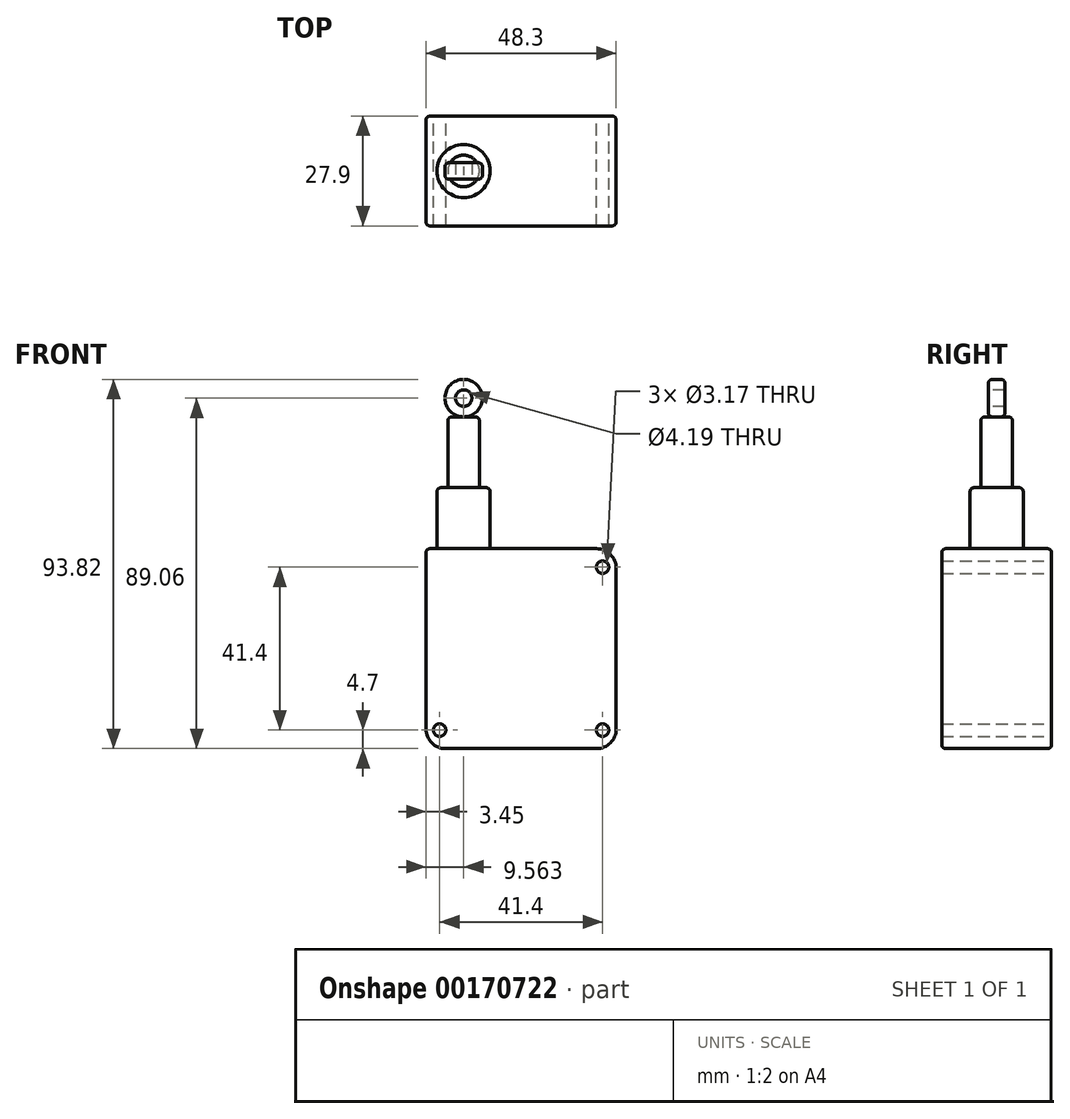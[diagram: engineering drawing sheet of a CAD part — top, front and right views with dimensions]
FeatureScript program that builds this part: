
annotation { "Feature Type Name" : "Feature", "Feature Type Description" : "" }
export const myFeature = defineFeature(function(context is Context, id is Id, definition is map)
    precondition{}
    {
        {
            var Q0;
            Q0=qCreatedBy(makeId("Front.planeOp"),FACE);
            var sketch = newSketch(context, id + "F0", { "sketchPlane" : qUnion([Q0])});
            skLineSegment(sketch, "E0.bottom", {"start": v(24.15, 25.4) * mm, "end": v(-24.15, 25.4) * mm});
            skLineSegment(sketch, "E0.top", {"start": v(24.15, -25.4) * mm, "end": v(-24.15, -25.4) * mm});
            skLineSegment(sketch, "E0.left", {"start": v(24.15, 25.4) * mm, "end": v(24.15, -25.4) * mm});
            skLineSegment(sketch, "E0.right", {"start": v(-24.15, 25.4) * mm, "end": v(-24.15, -25.4) * mm});
            skPoint(sketch, "E0.middle", {"position": v(0, 0) * mm});
            skLineSegment(sketch, "E1.bottom", {"start": v(20.7, 20.7) * mm, "end": v(-20.7, 20.7) * mm});
            skLineSegment(sketch, "E1.top", {"start": v(20.7, -20.7) * mm, "end": v(-20.7, -20.7) * mm});
            skLineSegment(sketch, "E1.left", {"start": v(20.7, 20.7) * mm, "end": v(20.7, -20.7) * mm});
            skLineSegment(sketch, "E1.right", {"start": v(-20.7, 20.7) * mm, "end": v(-20.7, -20.7) * mm});
            skCircle(sketch, "E2", {"center": v(20.7, -20.7) * mm, "radius": 1.59 * mm});
            skCircle(sketch, "E3", {"center": v(-20.7, -20.7) * mm, "radius": 1.59 * mm});
            skCircle(sketch, "E4", {"center": v(20.7, 20.7) * mm, "radius": 1.59 * mm});
            skLineSegment(sketch, "E5", {"start": v(-14.6, -30.38) * mm, "end": v(-14.6, 42.52) * mm});
            skSolve(sketch);
        }
        {
            var Q0;
            Q0 = qSketchRegion(id + "F0", true);
            var Q1;
            {var subQ3=sQuery(id+"F0.wireOp",EDGE,"E1.right");var subQ5=sQuery(id+"F0.wireOp",EDGE,"E1.bottom");var subQ6=makeQuery(id+"F0.imprint","INTERSECT",VERTEX,{"derivedFrom":[subQ5,subQ3]});Q1=makeQuery(id+"F0.imprint","IMPRINT",FACE,{"disambiguationData":[TD([[makeQuery(id+"F0.imprint","IMPRINT",EDGE,{"disambiguationData":[TD([[subQ6,1.0]])],"derivedFrom":subQ5}),1.0]])]});}
            var Q2;
            {var subQ5=sQuery(id+"F0.wireOp",EDGE,"E4");var subQ7=sQuery(id+"F0.wireOp",EDGE,"E1.bottom");var subQ8=makeQuery(id+"F0.imprint","INTERSECT",VERTEX,{"derivedFrom":[subQ7,subQ5]});Q2=makeQuery(id+"F0.imprint","IMPRINT",FACE,{"disambiguationData":[TD([[makeQuery(id+"F0.imprint","IMPRINT",EDGE,{"disambiguationData":[TD([[subQ8,-1.0]])],"derivedFrom":subQ7}),1.0]])]});}
            extrude(context, id + "F1", {"entities" : qUnion([Q0, Q1, Q2]), "depth" : 27.9 * mm});
        }
        {
            var Q0;
            Q0=makeQuery(id+"F1.opExtrude","SWEPT_FACE",FACE,{"disambiguationData":[OSD([sQuery(id+"F0.wireOp",EDGE,"E0.bottom")])]});
            var sketch = newSketch(context, id + "F2", { "sketchPlane" : qUnion([Q0])});
            skLineSegment(sketch, "E6", {"start": v(-14.6, 19.18) * mm, "end": v(-14.6, -45.39) * mm});
            skLineSegment(sketch, "E7", {"start": v(24.15, -13.95) * mm, "end": v(-48.5, -13.95) * mm});
            skPoint(sketch, "E7.endSnap0", {"position": v(24.15, -13.95) * mm});
            skCircle(sketch, "E8", {"center": v(-14.6, -13.95) * mm, "radius": 6.75 * mm});
            skSolve(sketch);
        }
        {
            var Q0;
            {var subQ0=sQuery(id+"F2.wireOp",EDGE,"E8");var subQ1=sQuery(id+"F2.wireOp",EDGE,"E6");var subQ2=makeQuery(id+"F2.imprint","INTERSECT",VERTEX,{"disambiguationData":[OD(0.0)],"derivedFrom":[subQ1,subQ0]});Q0=makeQuery(id+"F2.imprint","IMPRINT",FACE,{"disambiguationData":[TD([[makeQuery(id+"F2.imprint","IMPRINT",EDGE,{"disambiguationData":[TD([[subQ2,-1.0]])],"derivedFrom":subQ1}),-1.0]])]});}
            var Q1;
            {var subQ0=sQuery(id+"F2.wireOp",EDGE,"E8");var subQ1=sQuery(id+"F2.wireOp",EDGE,"E6");var subQ2=makeQuery(id+"F2.imprint","INTERSECT",VERTEX,{"disambiguationData":[OD(0.0)],"derivedFrom":[subQ1,subQ0]});Q1=makeQuery(id+"F2.imprint","IMPRINT",FACE,{"disambiguationData":[TD([[makeQuery(id+"F2.imprint","IMPRINT",EDGE,{"disambiguationData":[TD([[subQ2,-1.0]])],"derivedFrom":subQ1}),1.0]])]});}
            var Q2;
            {var subQ0=sQuery(id+"F2.wireOp",EDGE,"E7");var subQ1=sQuery(id+"F2.wireOp",EDGE,"E6");var subQ2=makeQuery(id+"F2.imprint","INTERSECT",VERTEX,{"derivedFrom":[subQ1,subQ0]});Q2=makeQuery(id+"F2.imprint","IMPRINT",FACE,{"disambiguationData":[TD([[makeQuery(id+"F2.imprint","IMPRINT",EDGE,{"disambiguationData":[TD([[subQ2,-1.0]])],"derivedFrom":subQ1}),1.0]])]});}
            var Q3;
            {var subQ0=sQuery(id+"F2.wireOp",EDGE,"E7");var subQ1=sQuery(id+"F2.wireOp",EDGE,"E6");var subQ2=makeQuery(id+"F2.imprint","INTERSECT",VERTEX,{"derivedFrom":[subQ1,subQ0]});Q3=makeQuery(id+"F2.imprint","IMPRINT",FACE,{"disambiguationData":[TD([[makeQuery(id+"F2.imprint","IMPRINT",EDGE,{"disambiguationData":[TD([[subQ2,-1.0]])],"derivedFrom":subQ1}),-1.0]])]});}
            extrude(context, id + "F3", {"entities" : qUnion([Q0, Q1, Q2, Q3]), "operationType" : NewBodyOperationType.ADD, "depth" : 15.5 * mm});
        }
        {
            var Q0;
            Q0=makeQuery(id+"F3.opExtrude","CAP_FACE",FACE,{"disambiguationData":[OSD([sQuery(id+"F2.wireOp",EDGE,"E8")])],"isStart":false});
            var sketch = newSketch(context, id + "F4", { "sketchPlane" : qUnion([Q0])});
            skPoint(sketch, "E9.middle", {"position": v(-14.6, -13.95) * mm});
            skCircle(sketch, "E10", {"center": v(-14.6, -13.95) * mm, "radius": 4 * mm});
            skSolve(sketch);
        }
        {
            var Q0;
            Q0=makeQuery(id+"F4.imprint","IMPRINT",FACE,{"disambiguationData":[TD([[makeQuery(id+"F4.imprint","IMPRINT",EDGE,{"derivedFrom":sQuery(id+"F4.wireOp",EDGE,"E9.bottom")}),1.0]])]});
            var Q1;
            Q1=makeQuery(id+"F4.imprint","IMPRINT",FACE,{"disambiguationData":[TD([[makeQuery(id+"F4.imprint","IMPRINT",EDGE,{"derivedFrom":sQuery(id+"F4.wireOp",EDGE,"E10")}),1.0]])]});
            extrude(context, id + "F5", {"entities" : qUnion([Q0, Q1]), "operationType" : NewBodyOperationType.ADD, "depth" : 18 * mm});
        }
        {
            var Q0;
            Q0=makeQuery(id+"F1.opExtrude","SWEPT_EDGE",EDGE,{"disambiguationData":[OSD([sQuery(id+"F0.wireOp",EDGE,"E0.bottom"),sQuery(id+"F0.wireOp",EDGE,"E0.left")])]});
            var Q1;
            Q1=makeQuery(id+"F1.opExtrude","SWEPT_EDGE",EDGE,{"disambiguationData":[OSD([sQuery(id+"F0.wireOp",EDGE,"E0.top"),sQuery(id+"F0.wireOp",EDGE,"E0.left")])]});
            var Q2;
            Q2=makeQuery(id+"F1.opExtrude","SWEPT_EDGE",EDGE,{"disambiguationData":[OSD([sQuery(id+"F0.wireOp",EDGE,"E0.top"),sQuery(id+"F0.wireOp",EDGE,"E0.right")])]});
            fillet(context, id + "F6", {"entities" : qUnion([Q0, Q1, Q2]), "radius" : 5 * mm, "tangentPropagation" : true, "allowEdgeOverflow" : false});
        }
        {
            var Q0;
            Q0=makeQuery(id+"F1.opExtrude","SWEPT_EDGE",EDGE,{"disambiguationData":[OSD([sQuery(id+"F0.wireOp",EDGE,"E0.bottom"),sQuery(id+"F0.wireOp",EDGE,"E0.right")])]});
            fillet(context, id + "F7", {"entities" : qUnion([Q0]), "radius" : 1 * mm, "tangentPropagation" : true, "allowEdgeOverflow" : false});
        }
        {
            var Q0;
            Q0=makeQuery(id+"F3.opExtrude","CAP_EDGE",EDGE,{"disambiguationData":[OSD([sQuery(id+"F2.wireOp",EDGE,"E8")])],"isStart":false});
            var Q1;
            Q1=makeQuery(id+"F1.opExtrude","CAP_EDGE",EDGE,{"disambiguationData":[OSD([sQuery(id+"F0.wireOp",EDGE,"E0.bottom")])],"isStart":false});
            var Q2;
            Q2=makeQuery(id+"F1.opExtrude","CAP_EDGE",EDGE,{"disambiguationData":[OSD([sQuery(id+"F0.wireOp",EDGE,"E0.bottom")])],"isStart":true});
            var Q3;
            Q3=makeQuery(id+"F1.opExtrude","CAP_EDGE",EDGE,{"disambiguationData":[OSD([sQuery(id+"F0.wireOp",EDGE,"E0.top")])],"isStart":false});
            var Q4;
            Q4=makeQuery(id+"F1.opExtrude","CAP_EDGE",EDGE,{"disambiguationData":[OSD([sQuery(id+"F0.wireOp",EDGE,"E0.top")])],"isStart":true});
            var Q5;
            Q5=makeQuery(id+"F1.opExtrude","CAP_EDGE",EDGE,{"disambiguationData":[OSD([sQuery(id+"F0.wireOp",EDGE,"E0.left")])],"isStart":false});
            var Q6;
            Q6=makeQuery(id+"F1.opExtrude","CAP_EDGE",EDGE,{"disambiguationData":[OSD([sQuery(id+"F0.wireOp",EDGE,"E0.right")])],"isStart":false});
            var Q7;
            Q7=makeQuery(id+"F1.opExtrude","CAP_EDGE",EDGE,{"disambiguationData":[OSD([sQuery(id+"F0.wireOp",EDGE,"E0.right")])],"isStart":true});
            var Q8;
            Q8=makeQuery(id+"F1.opExtrude","CAP_EDGE",EDGE,{"disambiguationData":[OSD([sQuery(id+"F0.wireOp",EDGE,"E0.left")])],"isStart":true});
            fillet(context, id + "F8", {"entities" : qUnion([Q0, Q1, Q2, Q3, Q4, Q5, Q6, Q7, Q8]), "radius" : 1 * mm, "tangentPropagation" : true, "allowEdgeOverflow" : false});
        }
        {
            var Q0;
            Q0=makeQuery(id+"F5.opExtrude","CAP_FACE",FACE,{"disambiguationData":[OSD([sQuery(id+"F4.wireOp",EDGE,"E10")])],"isStart":false});
            var sketch = newSketch(context, id + "F9", { "sketchPlane" : qUnion([Q0])});
            skLineSegment(sketch, "E11", {"start": v(-14.6, -13.95) * mm, "end": v(-10.6, -13.95) * mm});
            skLineSegment(sketch, "E12", {"start": v(-14.6, -13.95) * mm, "end": v(-18.6, -13.95) * mm});
            skSolve(sketch);
        }
        {
            var Q0;
            {var subQ0=sQuery(id+"F0.wireOp",EDGE,"E0.bottom");Q0=makeQuery(id+"F6.opFillet","BLEND_EDGE",EDGE,{"blendedFrom":[makeQuery(id+"F1.opExtrude","SWEPT_EDGE",EDGE,{"disambiguationData":[OSD([subQ0,sQuery(id+"F0.wireOp",EDGE,"E0.left")])]}),makeQuery(id+"F1.opExtrude","SWEPT_FACE",FACE,{"disambiguationData":[OSD([subQ0])]})],"blendedInto":[makeQuery(id+"F1.opExtrude","SWEPT_FACE",FACE,{"disambiguationData":[OSD([subQ0])]})]});}
            cPoint(context, id + "F10", {"entities" : qUnion([Q0]), "parameter" : 0.5});
        }
        {
            var Q0;
            Q0=sQuery(id+"F9.wireOp",VERTEX,"E11.end");
            var Q1;
            Q1=sQuery(id+"F9.wireOp",VERTEX,"E12.end");
            var Q2;
            Q2 = qCreatedBy(id + "F10" ,VERTEX);
            cPlane(context, id + "F11", {"entities" : qUnion([Q0, Q1, Q2]), "cplaneType" : CPlaneType.THREE_POINT, "offset" : 25.4 * mm, "width" : 152.4 * mm, "height" : 152.4 * mm});
        }
        {
            var Q0;
            Q0=qCreatedBy(id+"F11.planeOp",FACE);
            var sketch = newSketch(context, id + "F12", { "sketchPlane" : qUnion([Q0])});
            skCircle(sketch, "E13", {"center": v(14.59, 63.66) * mm, "radius": 4.76 * mm});
            skCircle(sketch, "E14", {"center": v(14.59, 63.66) * mm, "radius": 2.1 * mm});
            skSolve(sketch);
        }
        {
            var Q0;
            Q0=makeQuery(id+"F12.imprint","IMPRINT",FACE,{"disambiguationData":[TD([[makeQuery(id+"F12.imprint","IMPRINT",EDGE,{"derivedFrom":sQuery(id+"F12.wireOp",EDGE,"E13")}),1.0]])]});
            extrude(context, id + "F13", {"entities" : qUnion([Q0]), "operationType" : NewBodyOperationType.ADD, "endBound" : BoundingType.SYMMETRIC, "depth" : 4.2 * mm});
        }
        {
            var Q0;
            Q0=makeQuery(id+"F13.boolean.opBoolean","SPLIT",EDGE,{"derivedFrom":makeQuery(id+"F13.opExtrude","CAP_EDGE",EDGE,{"disambiguationData":[OSD([sQuery(id+"F12.wireOp",EDGE,"E13")])],"isStart":true})});
            var Q1;
            Q1=makeQuery(id+"F13.boolean.opBoolean","SPLIT",EDGE,{"derivedFrom":makeQuery(id+"F13.opExtrude","CAP_EDGE",EDGE,{"disambiguationData":[OSD([sQuery(id+"F12.wireOp",EDGE,"E13")])],"isStart":false})});
            var Q2;
            Q2=makeQuery(id+"F5.opExtrude","CAP_EDGE",EDGE,{"disambiguationData":[OSD([sQuery(id+"F4.wireOp",EDGE,"E10")])],"isStart":false});
            fillet(context, id + "F14", {"entities" : qUnion([Q0, Q1, Q2]), "radius" : 1 * mm, "tangentPropagation" : true, "allowEdgeOverflow" : false});
        }
    });
